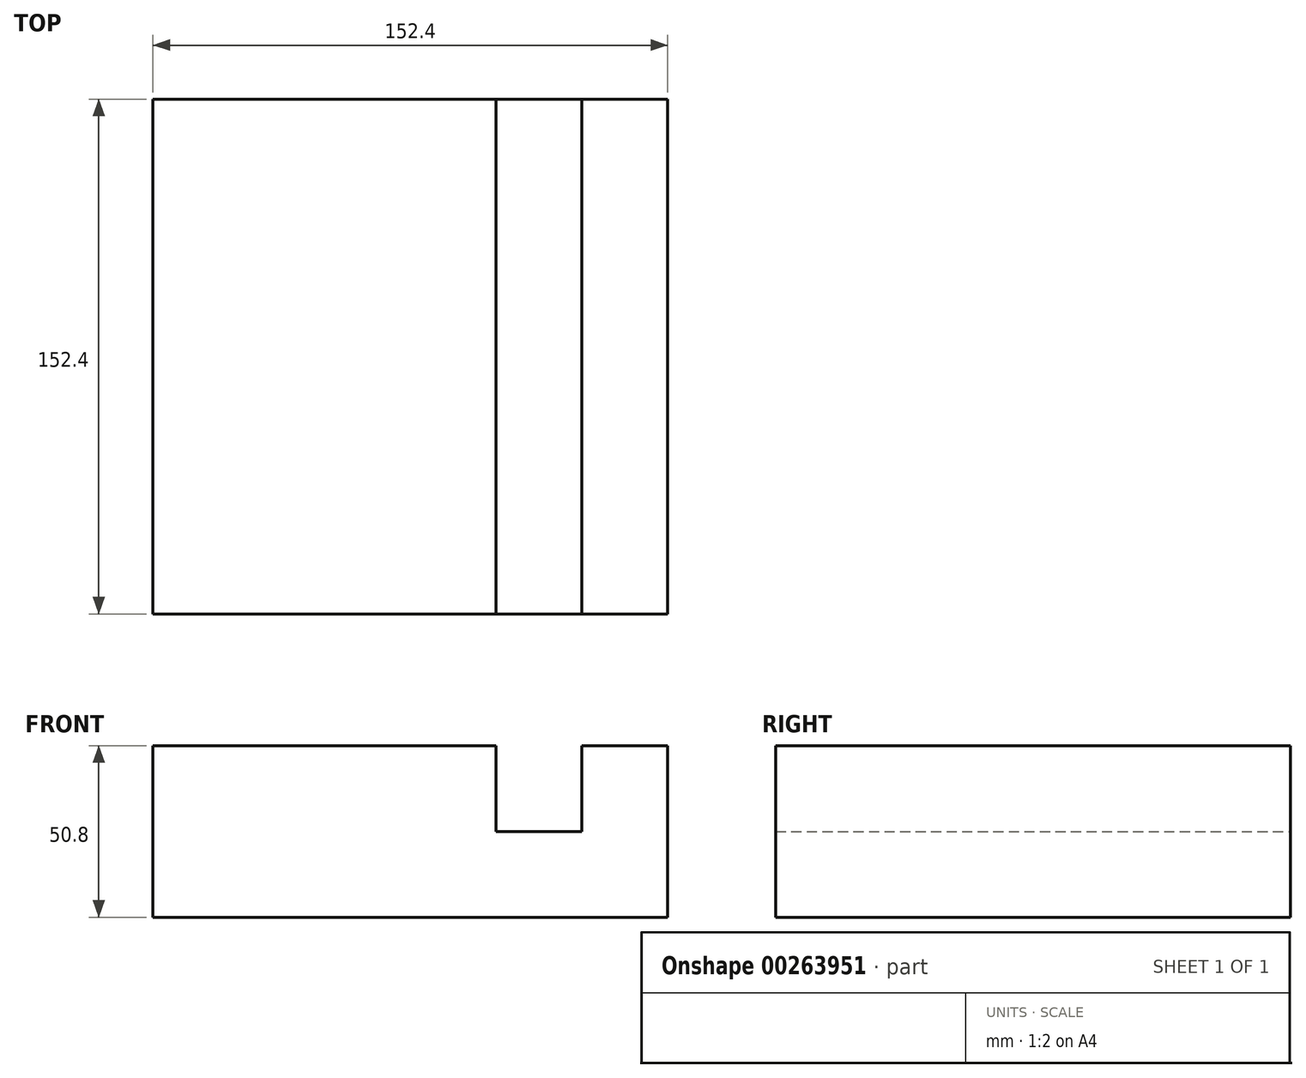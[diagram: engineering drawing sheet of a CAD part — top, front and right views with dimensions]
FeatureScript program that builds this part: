
annotation { "Feature Type Name" : "Feature", "Feature Type Description" : "" }
export const myFeature = defineFeature(function(context is Context, id is Id, definition is map)
    precondition{}
    {
        {
            var Q0;
            Q0=qCreatedBy(makeId("Front.planeOp"),FACE);
            var sketch = newSketch(context, id + "F0", { "sketchPlane" : qUnion([Q0])});
            skLineSegment(sketch, "E0", {"start": v(-75.98, 0) * mm, "end": v(76.42, 0) * mm});
            skLineSegment(sketch, "E1", {"start": v(76.42, 0) * mm, "end": v(76.42, 50.8) * mm});
            skLineSegment(sketch, "E2", {"start": v(51.02, 50.8) * mm, "end": v(76.42, 50.8) * mm});
            skLineSegment(sketch, "E3", {"start": v(51.02, 50.8) * mm, "end": v(51.02, 25.4) * mm});
            skLineSegment(sketch, "E4", {"start": v(25.62, 25.4) * mm, "end": v(51.02, 25.4) * mm});
            skLineSegment(sketch, "E5", {"start": v(25.62, 25.4) * mm, "end": v(25.62, 50.8) * mm});
            skLineSegment(sketch, "E6", {"start": v(25.62, 50.8) * mm, "end": v(-75.98, 50.8) * mm});
            skLineSegment(sketch, "E7", {"start": v(-75.98, 50.8) * mm, "end": v(-75.98, 0) * mm});
            skSolve(sketch);
        }
        {
            var Q0;
            Q0 = qSketchRegion(id + "F0", true);
            extrude(context, id + "F1", {"entities" : qUnion([Q0]), "depth" : 152.4 * mm});
        }
    });
